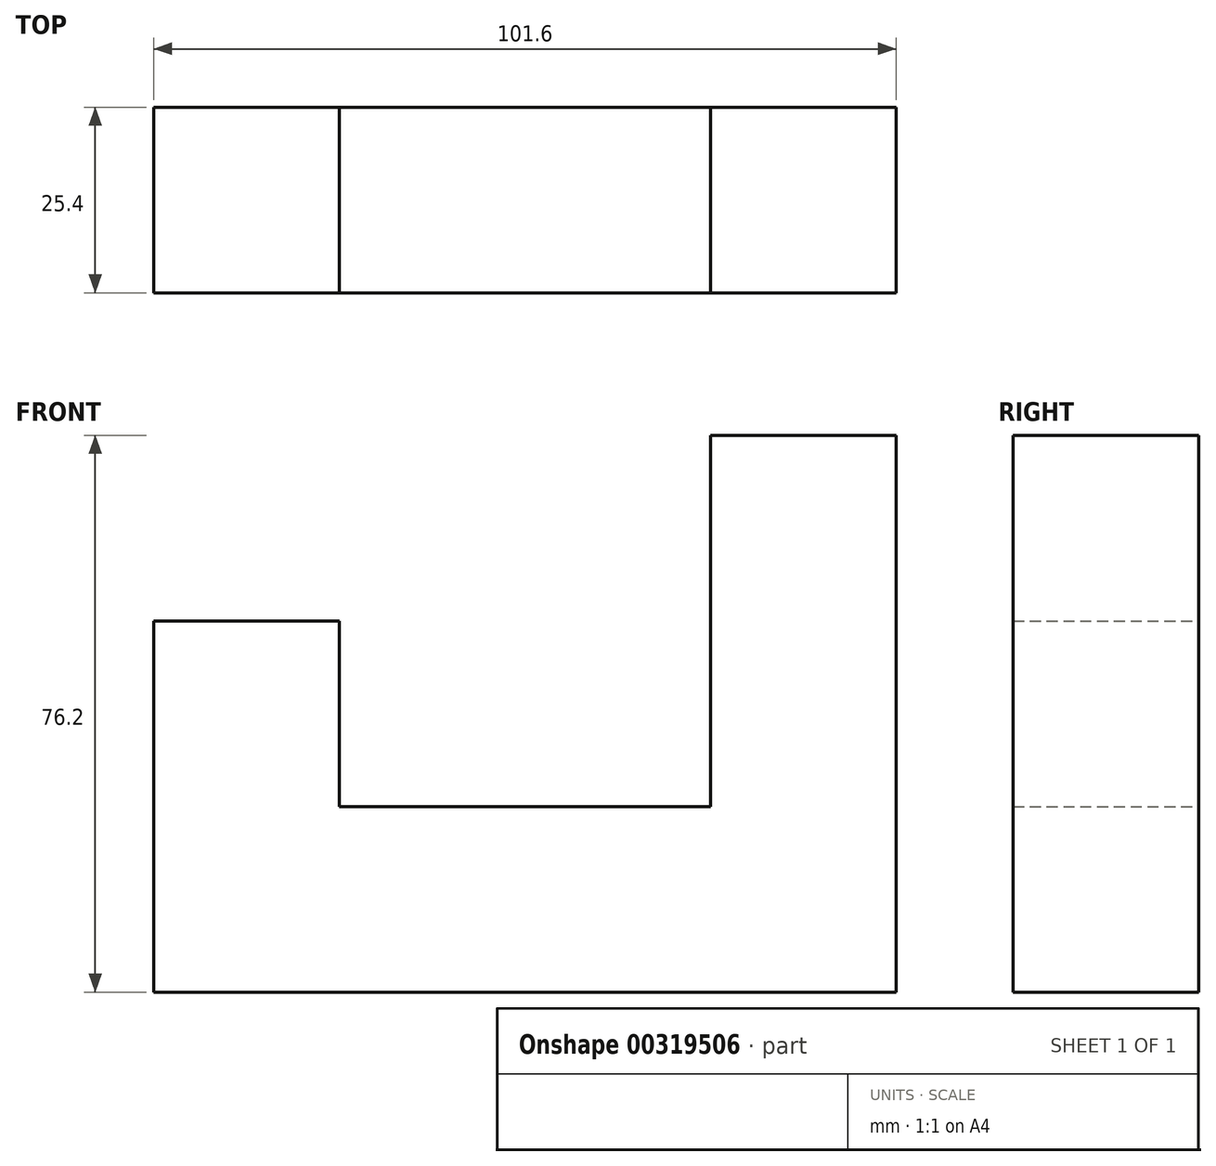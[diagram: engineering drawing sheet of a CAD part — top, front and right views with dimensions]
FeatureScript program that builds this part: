
annotation { "Feature Type Name" : "Feature", "Feature Type Description" : "" }
export const myFeature = defineFeature(function(context is Context, id is Id, definition is map)
    precondition{}
    {
        {
            var Q0;
            Q0=qCreatedBy(makeId("Front.planeOp"),FACE);
            var sketch = newSketch(context, id + "F0", { "sketchPlane" : qUnion([Q0])});
            skLineSegment(sketch, "E0", {"start": v(-66.2, -42.07) * mm, "end": v(35.4, -42.07) * mm});
            skLineSegment(sketch, "E1", {"start": v(35.4, -42.07) * mm, "end": v(35.4, 34.13) * mm});
            skLineSegment(sketch, "E2", {"start": v(35.4, 34.13) * mm, "end": v(10, 34.13) * mm});
            skLineSegment(sketch, "E3", {"start": v(10, 34.13) * mm, "end": v(10, -16.67) * mm});
            skLineSegment(sketch, "E4", {"start": v(10, -16.67) * mm, "end": v(-40.8, -16.67) * mm});
            skLineSegment(sketch, "E5", {"start": v(-40.8, -16.67) * mm, "end": v(-40.8, 8.73) * mm});
            skLineSegment(sketch, "E6", {"start": v(-40.8, 8.73) * mm, "end": v(-66.2, 8.73) * mm});
            skLineSegment(sketch, "E7", {"start": v(-66.2, 8.73) * mm, "end": v(-66.2, -42.07) * mm});
            skSolve(sketch);
        }
        {
            var Q0;
            Q0=makeQuery(id+"F0.imprint","IMPRINT",FACE,{"disambiguationData":[TD([[makeQuery(id+"F0.imprint","IMPRINT",EDGE,{"derivedFrom":sQuery(id+"F0.wireOp",EDGE,"E0")}),1.0]])]});
            extrude(context, id + "F1", {"entities" : qUnion([Q0]), "depth" : 25.4 * mm});
        }
    });
